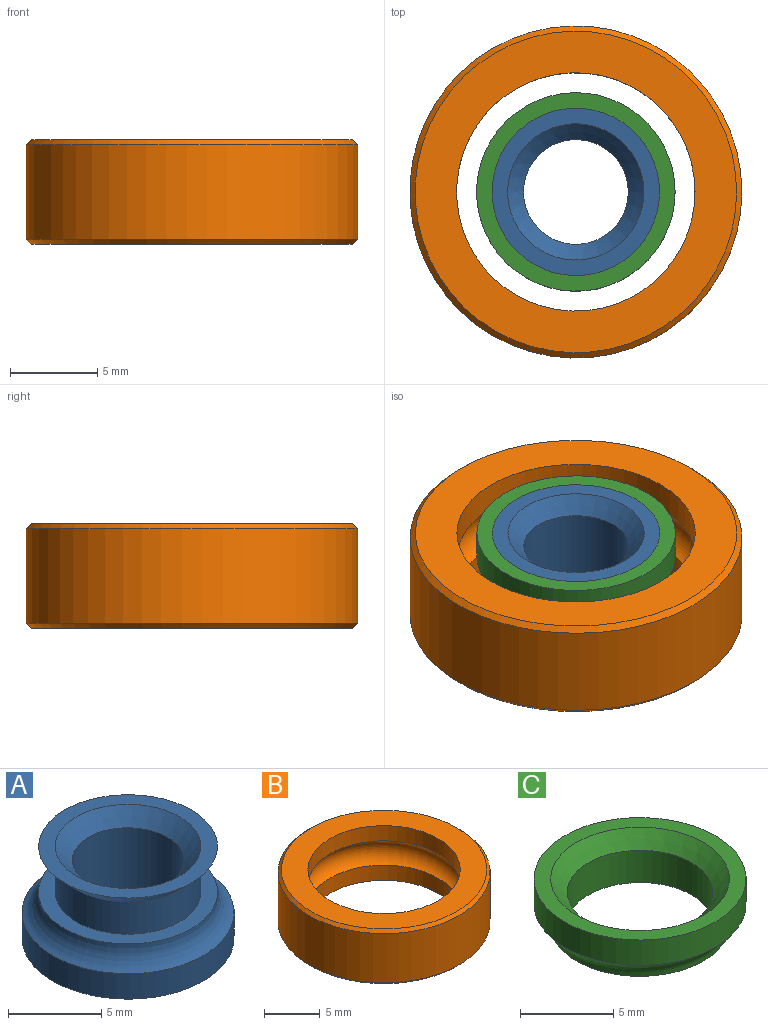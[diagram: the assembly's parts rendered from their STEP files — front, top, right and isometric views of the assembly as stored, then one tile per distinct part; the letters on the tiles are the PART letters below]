
ASSEMBLY  parts=3 mates=2
PART A: 10 faces, bbox 13.5x13.5x6 mm
  f0: plane 9.58x9.58mm, normal (0,0,1), area 24.3mm2, adj f1,f9
  f1: cone r=3.9mm half-angle=45deg, axis (0,0,1), area 34.3mm2, adj f0,f2
  f2: cylinder r=3.9mm len=7.8mm, axis (0,0,1), area 51.7mm2, adj f1,f3
  f3: plane 9.6x9.6mm, normal (0,0,1), area 24.6mm2, adj f2,f4
  f4: torus R=6.25mm, axis (0,0,1), area 54.3mm2, adj f3,f5
  f5: cylinder r=5.68mm len=11.36mm, axis (0,0,1), area 59.5mm2, adj f4,f6
  f6: plane 11.36x11.36mm, normal (0,0,-1), area 67.1mm2, adj f5,f7
  f7: cone r=3mm half-angle=45deg, axis (0,0,-1), area 8.4mm2, adj f6,f8
  f8: cylinder r=3mm len=6mm, axis (0,0,1), area 90.5mm2, adj f7,f9
  f9: cone r=3.9mm half-angle=45deg, axis (0,0,1), area 27.6mm2, adj f0,f8
PART B: 8 faces, bbox 19x19x6 mm
  f0: cone r=9.5mm half-angle=45deg, axis (0,0,-1), area 24.9mm2, adj f1,f7
  f1: cylinder r=9.5mm len=19mm, axis (0,0,1), area 322.3mm2, adj f0,f2
  f2: cone r=9.2mm half-angle=45deg, axis (0,0,1), area 24.9mm2, adj f1,f3
  f3: plane 18.4x18.4mm, normal (0,0,-1), area 119.7mm2, adj f2,f4
  f4: cylinder r=6.82mm len=13.64mm, axis (0,0,1), area 71.4mm2, adj f3,f5
  f5: torus R=6.25mm, axis (0,0,1), area 157.1mm2, adj f4,f6
  f6: cylinder r=6.82mm len=13.64mm, axis (0,0,1), area 71.4mm2, adj f5,f7
  f7: plane 18.4x18.4mm, normal (0,0,1), area 119.7mm2, adj f0,f6
PART C: 6 faces, bbox 13.5x13.5x4 mm
  f0: plane 11.36x11.36mm, normal (0,0,1), area 29.2mm2, adj f1,f5
  f1: cone r=4.79mm half-angle=45deg, axis (0,0,1), area 34.3mm2, adj f0,f2
  f2: cylinder r=3.9mm len=7.8mm, axis (0,0,1), area 51.7mm2, adj f1,f3
  f3: plane 9.6x9.6mm, normal (0,0,-1), area 24.6mm2, adj f2,f4
  f4: torus R=6.25mm, axis (0,0,1), area 54.3mm2, adj f3,f5
  f5: cylinder r=5.68mm len=11.36mm, axis (0,0,1), area 59.5mm2, adj f0,f4
PLACE A at identity
PLACE B at identity
PLACE C at identity
MATE revolute C.f1 <-> B.f0  axis (0,0,1) through (0,0,3)mm
MATE fastened A.f1 <-> C.f1  axis (0,0,1) through (0,0,3)mm
